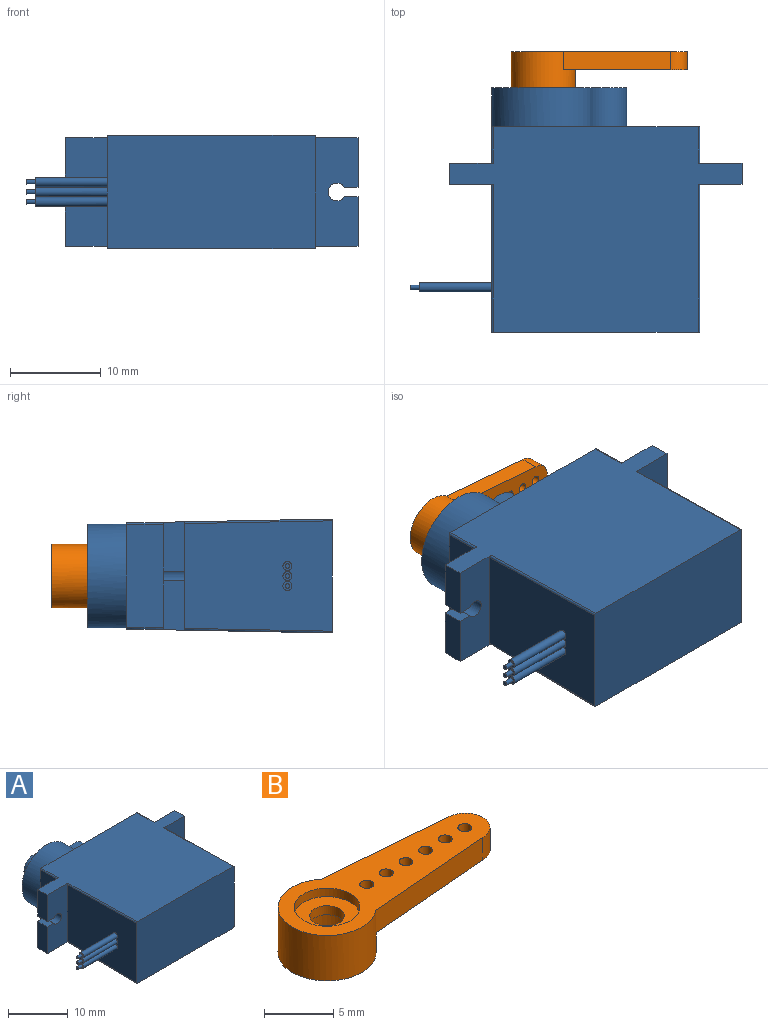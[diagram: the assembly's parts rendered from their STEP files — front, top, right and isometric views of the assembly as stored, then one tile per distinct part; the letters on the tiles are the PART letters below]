
ASSEMBLY  parts=2 mates=1
PART A: 49 faces, bbox 36.7x30x12.6 mm
  f0: plane 5.44x2.32mm, normal (-1,0,0), area 12.6mm2, adj f1,f10,f26,f39
  f1: plane 11.97x4.84mm, normal (0,-1,0), area 51mm2, adj f0,f4,f13,f24,f25,f26,f39,f40
  f2: plane 5.44x2.32mm, normal (1,0,0), area 12.6mm2, adj f3,f6,f22,f40
  f3: plane 11.97x4.84mm, normal (0,-1,0), area 51mm2, adj f2,f5,f12,f21,f22,f23,f39,f40
  f4: plane 16.34x12.19mm, normal (-1,0,0), area 191.7mm2, adj f1,f11,f27,f28,f29,f41,f45
  f5: plane 16.34x12.19mm, normal (1,0,0), area 194.1mm2, adj f3,f11,f42,f46
  f6: plane 11.88x4.84mm, normal (0,1,0), area 50.6mm2, adj f2,f7,f12,f21,f22,f23,f39,f40
  f7: plane 11.48x4.06mm, normal (1,0,0), area 46.3mm2, adj f6,f8,f43,f47
  f8: plane 23.03x11.73mm, normal (0,1,0), area 149.2mm2, adj f7,f9,f14,f15,f39,f40,f43,f44
  f9: plane 11.48x4.06mm, normal (-1,0,0), area 46.3mm2, adj f8,f10,f44,f48
  f10: plane 11.88x4.84mm, normal (0,1,0), area 50.6mm2, adj f0,f9,f13,f24,f25,f26,f39,f40
  f11: plane 23.03x12.59mm, normal (0,-1,0), area 289.9mm2, adj f4,f5,f39,f40,f41,f42,f45,f46
  f12: plane 5.44x2.32mm, normal (1,0,0), area 12.6mm2, adj f3,f6,f21,f39
  f13: plane 5.44x2.32mm, normal (-1,0,0), area 12.6mm2, adj f1,f10,f25,f40
  f14: cylinder r=5.73mm len=11.46mm, axis (0,-1,0), area 131.4mm2, adj f8,f15,f16
  f15: cylinder r=2.85mm len=5.7mm, axis (0,-1,0), area 49.4mm2, adj f8,f14,f16
  f16: plane 14.96x11.46mm, normal (0,1,0), area 104.1mm2, adj f14,f15,f18
  f17: cylinder r=0.9mm len=3.95mm, axis (0,-1,0), area 22.3mm2, adj f19,f20
  f18: cylinder r=2.3mm len=4.6mm, axis (0,-1,0), area 42.6mm2, adj f16,f19
  f19: plane 4.6x4.6mm, normal (0,1,0), area 14.1mm2, adj f17,f18
  f20: plane 1.8x1.8mm, normal (0,1,0), area 2.5mm2, adj f17
  f21: plane 2.32x1.51mm, normal (0,0,-1), area 3.5mm2, adj f3,f6,f12,f23
  f22: plane 2.32x1.51mm, normal (0,0,1), area 3.5mm2, adj f2,f3,f6,f23
  f23: cylinder r=0.98mm len=2.32mm, axis (0,1,0), area 11.6mm2, adj f3,f6,f21,f22
  f24: cylinder r=0.98mm len=2.32mm, axis (0,1,0), area 11.6mm2, adj f1,f10,f25,f26
  f25: plane 2.32x1.51mm, normal (0,0,1), area 3.5mm2, adj f1,f10,f13,f24
  f26: plane 2.32x1.51mm, normal (0,0,-1), area 3.5mm2, adj f0,f1,f10,f24
  f27: cylinder r=0.5mm len=8mm, axis (-1,0,0), area 25.1mm2, adj f4,f35
  f28: cylinder r=0.5mm len=8mm, axis (-1,0,0), area 25.1mm2, adj f4,f32
  f29: cylinder r=0.5mm len=8mm, axis (-1,0,0), area 25.1mm2, adj f4,f38
  f30: plane 0.5x0.5mm, normal (-1,0,0), area 0.2mm2, adj f31
  f31: cylinder r=0.25mm len=1mm, axis (-1,0,0), area 1.6mm2, adj f30,f32
  f32: plane 1x1mm, normal (-1,0,0), area 0.6mm2, adj f28,f31
  f33: plane 0.5x0.5mm, normal (-1,0,0), area 0.2mm2, adj f34
  f34: cylinder r=0.25mm len=1mm, axis (-1,0,0), area 1.6mm2, adj f33,f35
  f35: plane 1x1mm, normal (-1,0,0), area 0.6mm2, adj f27,f34
  f36: plane 0.5x0.5mm, normal (-1,0,0), area 0.2mm2, adj f37
  f37: cylinder r=0.25mm len=1mm, axis (-1,0,0), area 1.6mm2, adj f36,f38
  f38: plane 1x1mm, normal (-1,0,0), area 0.6mm2, adj f29,f37
  f39: plane 32.31x22.72mm, normal (0,0.02,1), area 536.7mm2, adj f0,f1,f3,f6,f8,f10,f11,f12
  f40: plane 32.31x22.72mm, normal (0,0.02,-1), area 536.7mm2, adj f1,f2,f3,f6,f8,f10,f11,f13
  f41: cylinder r=0.2mm len=16.35mm, axis (0,-1,-0.02), area 5.1mm2, adj f1,f4,f11,f40
  f42: cylinder r=0.2mm len=16.35mm, axis (0,1,0.02), area 5.1mm2, adj f3,f5,f11,f40
  f43: cylinder r=0.2mm len=4.07mm, axis (0,1,0.02), area 1.3mm2, adj f6,f7,f8,f40
  f44: cylinder r=0.2mm len=4.07mm, axis (0,-1,-0.02), area 1.3mm2, adj f8,f9,f10,f40
  f45: cylinder r=0.2mm len=16.35mm, axis (0,1,-0.02), area 5.1mm2, adj f1,f4,f11,f39
  f46: cylinder r=0.2mm len=16.35mm, axis (0,-1,0.02), area 5.1mm2, adj f3,f5,f11,f39
  f47: cylinder r=0.2mm len=4.07mm, axis (0,-1,0.02), area 1.3mm2, adj f6,f7,f8,f39
  f48: cylinder r=0.2mm len=4.07mm, axis (0,1,-0.02), area 1.3mm2, adj f8,f9,f10,f39
PART B: 18 faces, bbox 19.4x7.1x4 mm
  f0: cylinder r=1.25mm len=2.49mm, axis (0,0,-1), area 6.3mm2, adj f15,f17
  f1: plane 11.9x2mm, normal (0.08,1,0), area 23.9mm2, adj f8,f10,f11,f13
  f2: plane 11.9x2mm, normal (0.08,-1,0), area 23.9mm2, adj f8,f10,f11,f13
  f3: cylinder r=0.5mm len=2mm, axis (0,0,-1), area 6.3mm2, adj f10,f11
  f4: cylinder r=0.5mm len=2mm, axis (0,0,-1), area 6.3mm2, adj f10,f11
  f5: cylinder r=0.5mm len=2mm, axis (0,0,-1), area 6.3mm2, adj f10,f11
  f6: cylinder r=0.5mm len=2mm, axis (0,0,-1), area 6.3mm2, adj f10,f11
  f7: cylinder r=0.5mm len=2mm, axis (0,0,-1), area 6.3mm2, adj f10,f11
  f8: cylinder r=1.78mm len=3.56mm, axis (0,0,-1), area 11.2mm2, adj f1,f2,f10,f11
  f9: cylinder r=0.5mm len=2mm, axis (0,0,-1), area 6.3mm2, adj f10,f11
  f10: plane 19.41x7.07mm, normal (0,0,1), area 70.8mm2, adj f1,f2,f3,f4,f5,f6,f7,f8
  f11: plane 13.68x5.55mm, normal (0,0,-1), area 49.3mm2, adj f1,f2,f3,f4,f5,f6,f7,f8
  f12: cylinder r=2.38mm len=4.75mm, axis (0,0,-1), area 11.2mm2, adj f10,f15
  f13: cylinder r=3.54mm len=7.07mm, axis (0,0,-1), area 76.1mm2, adj f1,f2,f10,f11,f14
  f14: plane 7.07x7.07mm, normal (0,0,-1), area 21.5mm2, adj f13,f16
  f15: plane 4.75x4.75mm, normal (0,0,1), area 12.9mm2, adj f0,f12
  f16: cylinder r=2.38mm len=4.75mm, axis (0,0,-1), area 36.6mm2, adj f14,f17
  f17: plane 4.75x4.75mm, normal (0,0,-1), area 12.9mm2, adj f0,f16
PLACE A t=(-14.05,-22.45,-7.68)mm
PLACE B rot(axis=(-1,0,0),90deg) t=(-31.35,4.55,-1.39)mm
MATE revolute B.f16 <-> A.f14  axis (0,-1,0) through (-31.35,4.55,-1.39)mm
